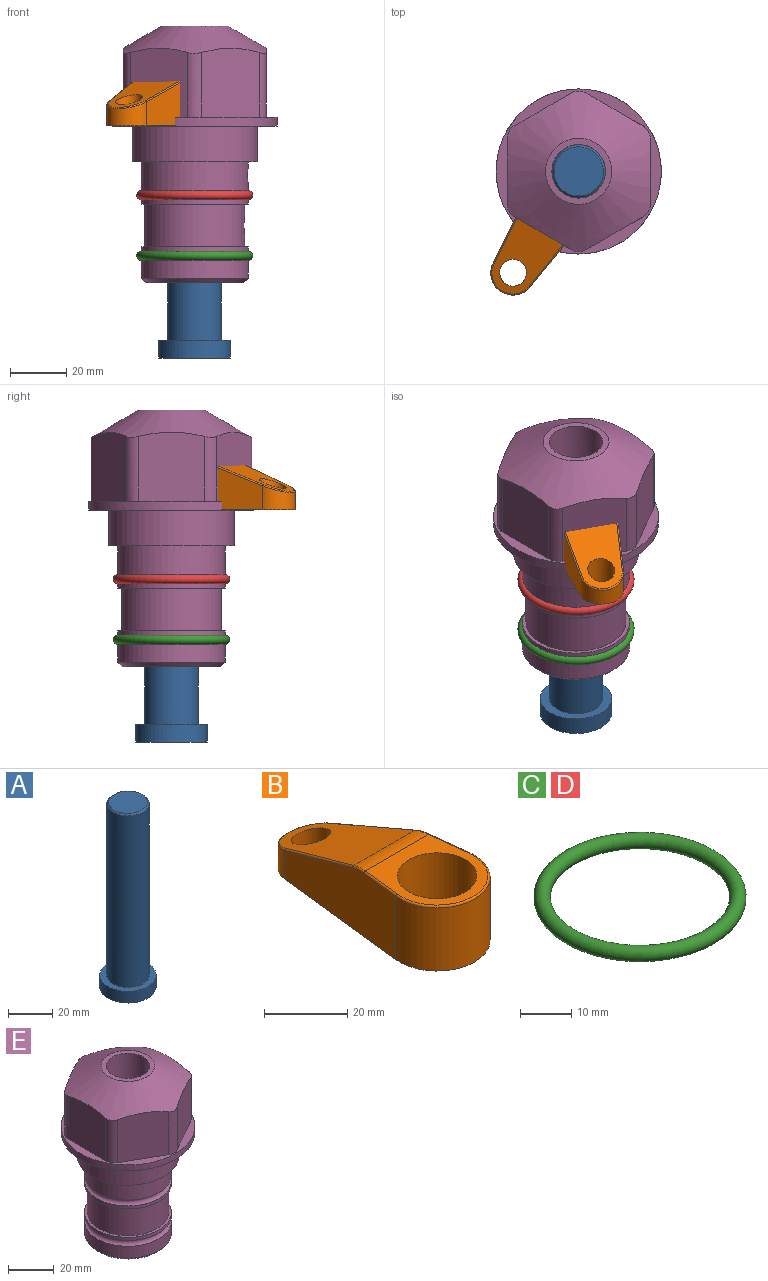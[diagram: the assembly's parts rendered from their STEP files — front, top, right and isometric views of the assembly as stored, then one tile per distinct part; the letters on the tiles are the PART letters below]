
ASSEMBLY  parts=5 mates=3
PART A: 6 faces, bbox 25.4x25.4x101.6 mm
  f0: plane 17.46x17.46mm, normal (0,0,1), area 239.5mm2, adj f5
  f1: plane 25.4x25.4mm, normal (0,0,-1), area 506.7mm2, adj f2
  f2: cylinder r=12.7mm len=25.4mm, axis (0,0,1), area 506.7mm2, adj f1,f3
  f3: plane 25.4x25.4mm, normal (0,0,1), area 221.7mm2, adj f2,f4
  f4: cylinder r=9.53mm len=94.46mm, axis (0,0,1), area 5653mm2, adj f3,f5
  f5: cone r=8.73mm half-angle=45deg, axis (0,0,-1), area 64.4mm2, adj f0,f4
PART B: 44 faces, bbox 27.5x64.5x19.1 mm
  f0: plane 2.3x0.95mm, normal (0,0,-1), area 1mm2, adj f25,f30,f34
  f1: plane 63.5x25.4mm, normal (0,0,-1), area 561.7mm2, adj f2,f3,f4,f5,f6,f7,f19,f20
  f2: cylinder r=12.7mm len=25.4mm, axis (0,0,-1), area 792.2mm2, adj f1,f3,f5,f13
  f3: plane 42.33x18.54mm, normal (0.99,0.11,0), area 647mm2, adj f1,f2,f4,f11,f12,f14
  f4: cylinder r=7.94mm len=15.78mm, axis (0,0,-1), area 158.6mm2, adj f1,f3,f5,f16
  f5: plane 42.33x18.54mm, normal (-0.99,0.11,0), area 647mm2, adj f1,f2,f4,f15,f17,f18
  f6: cylinder r=9.53mm len=19.05mm, axis (0,0,-1), area 1140.1mm2, adj f1,f8
  f7: cylinder r=4.76mm len=10.98mm, axis (0,0,-1), area 276.1mm2, adj f1,f9
  f8: plane 25.83x24.38mm, normal (0,0,1), area 262.2mm2, adj f6,f10,f11,f13,f15
  f9: plane 32.49x20.55mm, normal (0,0.34,0.94), area 489.9mm2, adj f7,f10,f14,f16,f18
  f10: cylinder r=12.7mm len=21.49mm, axis (-1,0,0), area 93.2mm2, adj f8,f9,f12,f17
  f11: cylinder r=0.51mm len=12.34mm, axis (0.11,-0.99,0), area 9.9mm2, adj f3,f8,f12,f13
  f12: bspline ~7.62x1.64mm, area 3.5mm2, adj f3,f10,f11,f14
  f13: torus R=12.19mm, axis (0,0,1), area 33.6mm2, adj f2,f8,f11,f15
  f14: cylinder r=0.51mm len=26.01mm, axis (0.1,-0.93,0.34), area 21.6mm2, adj f3,f9,f12,f16
  f15: cylinder r=0.51mm len=12.34mm, axis (0.11,0.99,0), area 9.9mm2, adj f5,f8,f13,f17
  f16: bspline ~15.78x7.05mm, area 15.7mm2, adj f4,f9,f14,f18
  f17: bspline ~7.62x1.64mm, area 3.5mm2, adj f5,f10,f15,f18
  f18: cylinder r=0.51mm len=26.01mm, axis (0.1,0.93,-0.34), area 21.6mm2, adj f5,f9,f16,f17
  f19: plane 21.6x14.29mm, normal (-0.99,-0.11,0), area 242.6mm2, adj f1,f26,f28,f34,f36,f38
  f20: plane 21.6x14.29mm, normal (0.99,-0.11,0), area 242.6mm2, adj f1,f27,f29,f37,f39,f41
  f21: cylinder r=12.7mm len=14.29mm, axis (0,0,-1), area 173.2mm2, adj f1,f26,f27,f30,f31,f33
  f22: cylinder r=7.94mm len=7.63mm, axis (0,0,-1), area 53.8mm2, adj f1,f28,f29,f42
  f23: plane 2.3x0.95mm, normal (0,0,-1), area 1mm2, adj f25,f33,f37
  f24: plane 17.94x12.32mm, normal (0,-0.34,-0.94), area 191.2mm2, adj f25,f38,f41,f42
  f25: cylinder r=9.53mm len=12.93mm, axis (-1,0,0), area 37.5mm2, adj f0,f23,f24,f31,f36,f39
  f26: cylinder r=1.59mm len=14.29mm, axis (0,0,-1), area 49mm2, adj f1,f19,f21,f32
  f27: cylinder r=1.59mm len=14.29mm, axis (0,0,-1), area 49mm2, adj f1,f20,f21,f35
  f28: cylinder r=1.59mm len=7.28mm, axis (0,0,-1), area 22.1mm2, adj f1,f19,f22,f40
  f29: cylinder r=1.59mm len=7.28mm, axis (0,0,-1), area 22.1mm2, adj f1,f20,f22,f43
  f30: torus R=14.29mm, axis (0,0,1), area 5.8mm2, adj f0,f21,f31,f32
  f31: bspline ~11.06x2.73mm, area 20.8mm2, adj f21,f25,f30,f33
  f32: sphere r=1.59mm, area 5.4mm2, adj f26,f30,f34
  f33: torus R=14.29mm, axis (0,0,1), area 5.8mm2, adj f21,f23,f31,f35
  f34: cylinder r=1.59mm len=1.68mm, axis (-0.11,0.99,0), area 2.4mm2, adj f0,f19,f32,f36
  f35: sphere r=1.59mm, area 5.4mm2, adj f27,f33,f37
  f36: bspline ~5.82x2.33mm, area 7.7mm2, adj f19,f25,f34,f38
  f37: cylinder r=1.59mm len=1.68mm, axis (0.11,0.99,0), area 2.4mm2, adj f20,f23,f35,f39
  f38: cylinder r=1.59mm len=18.33mm, axis (0.1,-0.93,0.34), area 46.7mm2, adj f19,f24,f36,f40
  f39: bspline ~5.82x2.33mm, area 7.7mm2, adj f20,f25,f37,f41
  f40: sphere r=1.59mm, area 3.6mm2, adj f28,f38,f42
  f41: cylinder r=1.59mm len=18.33mm, axis (0.1,0.93,-0.34), area 46.7mm2, adj f20,f24,f39,f43
  f42: bspline ~8.31x1.84mm, area 15.3mm2, adj f22,f24,f40,f43
  f43: sphere r=1.59mm, area 3.6mm2, adj f29,f41,f42
PART C: 1 faces, bbox 44.7x44.7x3.2 mm
  f0: torus R=19.05mm, axis (0,0,1), area 1193.9mm2
PART D: same geometry as C
PART E: 36 faces, bbox 58.7x58.7x91.2 mm
  f0: cylinder r=17.78mm len=35.56mm, axis (0,0,1), area 1670.8mm2, adj f23,f24,f31
  f1: cylinder r=19.05mm len=38.1mm, axis (0,0,1), area 1191.9mm2, adj f26,f27,f30
  f2: plane 58.66x58.66mm, normal (0,0,-1), area 1150.6mm2, adj f3,f28
  f3: cylinder r=29.33mm len=58.66mm, axis (0,0,-1), area 585.1mm2, adj f2,f4
  f4: plane 58.66x58.66mm, normal (0,0,1), area 475.9mm2, adj f3,f5,f6,f7,f8,f9,f10,f11
  f5: plane 24.5x20.32mm, normal (-0.5,0.87,0), area 562.8mm2, adj f4,f15,f16,f17
  f6: plane 24.5x20.32mm, normal (0.5,0.87,0), area 562.8mm2, adj f4,f14,f15,f17
  f7: plane 24.5x23.48mm, normal (1,0,0), area 562.8mm2, adj f4,f13,f14,f17
  f8: plane 24.5x20.32mm, normal (0.5,-0.87,0), area 562.8mm2, adj f4,f12,f13,f17
  f9: plane 24.5x20.32mm, normal (-0.5,-0.87,0), area 562.8mm2, adj f4,f11,f12,f17
  f10: plane 24.5x23.48mm, normal (-1,0,0), area 562.8mm2, adj f4,f11,f16,f17
  f11: cylinder r=5.08mm len=23.01mm, axis (0,0,-1), area 121.2mm2, adj f4,f9,f10,f17
  f12: cylinder r=5.08mm len=23.01mm, axis (0,0,-1), area 121.2mm2, adj f4,f8,f9,f17
  f13: cylinder r=5.08mm len=23.01mm, axis (0,0,-1), area 121.2mm2, adj f4,f7,f8,f17
  f14: cylinder r=5.08mm len=23.01mm, axis (0,0,-1), area 121.2mm2, adj f4,f6,f7,f17
  f15: cylinder r=5.08mm len=23.01mm, axis (0,0,-1), area 121.2mm2, adj f4,f5,f6,f17
  f16: cylinder r=5.08mm len=23.01mm, axis (0,0,-1), area 121.2mm2, adj f4,f5,f10,f17
  f17: cone r=11.73mm half-angle=60deg, axis (0,0,-1), area 2071.8mm2, adj f5,f6,f7,f8,f9,f10,f11,f12
  f18: plane 23.46x23.46mm, normal (0,0,1), area 147.4mm2, adj f17,f35
  f19: plane 34.93x34.93mm, normal (0,0,-1), area 958mm2, adj f29
  f20: cylinder r=19.05mm len=38.1mm, axis (0,0,1), area 760.1mm2, adj f21,f29
  f21: torus R=19.05mm, axis (0,0,1), area 565.3mm2, adj f20,f22
  f22: cylinder r=19.05mm len=38.1mm, axis (0,0,1), area 190mm2, adj f21,f23
  f23: plane 38.1x38.1mm, normal (0,0,1), area 146.9mm2, adj f0,f22
  f24: plane 38.1x38.1mm, normal (0,0,-1), area 146.9mm2, adj f0,f25
  f25: cylinder r=19.05mm len=38.1mm, axis (0,0,1), area 190mm2, adj f24,f26
  f26: torus R=19.05mm, axis (0,0,1), area 565.3mm2, adj f1,f25
  f27: plane 44.45x44.45mm, normal (0,0,-1), area 411.7mm2, adj f1,f28
  f28: cylinder r=22.23mm len=44.45mm, axis (0,0,1), area 1773.5mm2, adj f2,f27
  f29: cone r=19.05mm half-angle=45deg, axis (0,0,1), area 257.5mm2, adj f19,f20
  f30: cylinder r=3.17mm len=6.75mm, axis (-1,0,0), area 128mm2, adj f1,f33
  f31: cylinder r=3.17mm len=6.35mm, axis (-1,0,0), area 102.5mm2, adj f0,f33
  f32: plane 25.4x25.4mm, normal (0,0,1), area 506.7mm2, adj f33
  f33: cylinder r=12.7mm len=66.42mm, axis (0,0,-1), area 5236.2mm2, adj f30,f31,f32,f34
  f34: cone r=9.53mm half-angle=30deg, axis (0,0,-1), area 443.4mm2, adj f33,f35
  f35: cylinder r=9.53mm len=19.05mm, axis (0,0,-1), area 849mm2, adj f18,f34
PLACE A rot(axis=(0,0,-1),122.9deg) t=(0,0,-54.44)mm
PLACE B rot(axis=(0,0,1),147.1deg) t=(0,0,0.17)mm
PLACE C t=(0,0,-21.59)mm
PLACE D at identity
PLACE E at identity fixed
MATE fastened C.f0 <-> E.f0  axis (0,0,1) through (0,0,-46.1)mm
MATE cylindrical A.f2 <-> E.f0  axis (0,0,1) through (0,0,-28.8)mm
MATE fastened B.f2 <-> A.f2  axis (0,0,1) through (0,0,19.22)mm
